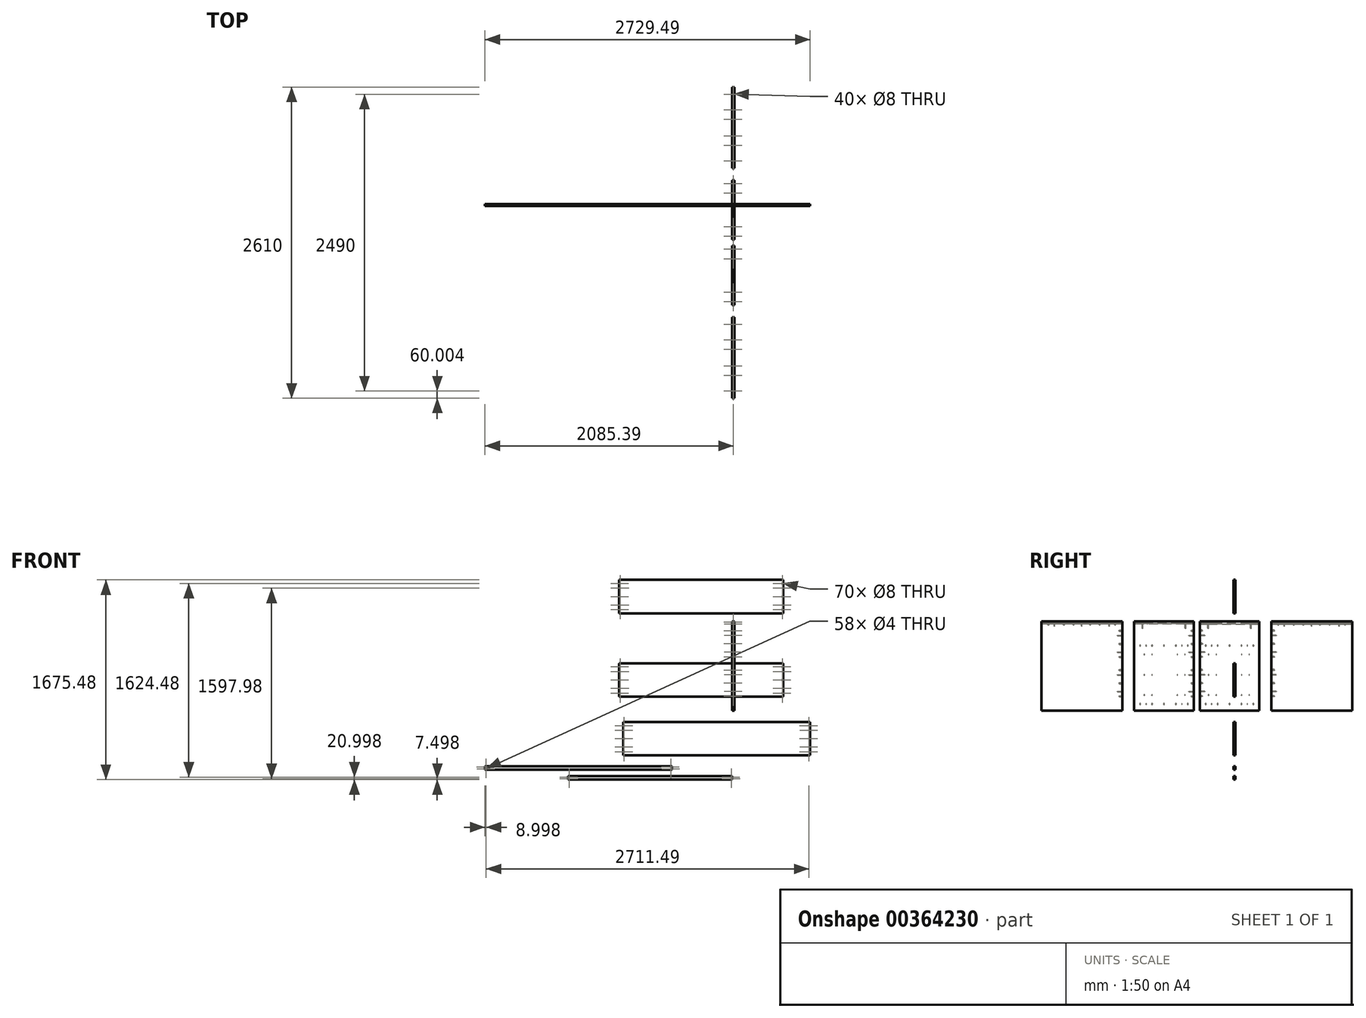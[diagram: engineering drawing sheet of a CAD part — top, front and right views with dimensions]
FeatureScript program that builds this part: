
annotation { "Feature Type Name" : "Feature", "Feature Type Description" : "" }
export const myFeature = defineFeature(function(context is Context, id is Id, definition is map)
    precondition{}
    {
        {
            var Q0;
            Q0=qCreatedBy(makeId("Right.planeOp"),FACE);
            var sketch = newSketch(context, id + "F0", { "sketchPlane" : qUnion([Q0])});
            skLineSegment(sketch, "E0.bottom", {"start": v(-300.67, 437.5) * mm, "end": v(199.33, 437.5) * mm});
            skLineSegment(sketch, "E0.top", {"start": v(-300.67, -312.5) * mm, "end": v(199.33, -312.5) * mm});
            skLineSegment(sketch, "E0.left", {"start": v(-300.67, 437.5) * mm, "end": v(-300.67, -312.5) * mm});
            skLineSegment(sketch, "E0.right", {"start": v(199.33, 437.5) * mm, "end": v(199.33, -312.5) * mm});
            skSolve(sketch);
        }
        {
            var Q0;
            Q0=makeQuery(id+"F0.imprint","IMPRINT",FACE,{"disambiguationData":[TD([[makeQuery(id+"F0.imprint","IMPRINT",EDGE,{"derivedFrom":sQuery(id+"F0.wireOp",EDGE,"E0.bottom")}),-1.0]])]});
            var sketch = newSketch(context, id + "F1", { "sketchPlane" : qUnion([Q0])});
            skLineSegment(sketch, "E1", {"start": v(-300.67, -257.5) * mm, "end": v(199.33, -257.5) * mm, "construction": true});
            skPoint(sketch, "E2", {"position": v(-250.67, -257.5) * mm});
            skPoint(sketch, "E3.1.0.0", {"position": v(-150.67, -257.5) * mm});
            skPoint(sketch, "E3.2.0.0", {"position": v(-50.67, -257.5) * mm});
            skPoint(sketch, "E3.3.0.0", {"position": v(49.33, -257.5) * mm});
            skPoint(sketch, "E3.4.0.0", {"position": v(149.33, -257.5) * mm});
            skLineSegment(sketch, "E3.direction1", {"start": v(-250.67, -257.5) * mm, "end": v(-150.67, -257.5) * mm, "construction": true});
            skPoint(sketch, "E4", {"position": v(99.33, -257.5) * mm});
            skPoint(sketch, "E5", {"position": v(-200.67, -257.5) * mm});
            skPoint(sketch, "E6.0.1.0", {"position": v(99.33, 232.5) * mm});
            skPoint(sketch, "E6.0.1.1", {"position": v(-150.67, 232.5) * mm});
            skPoint(sketch, "E6.0.1.2", {"position": v(-250.67, 232.5) * mm});
            skLineSegment(sketch, "E6.0.1.3", {"start": v(-300.67, 232.5) * mm, "end": v(199.33, 232.5) * mm, "construction": true});
            skPoint(sketch, "E6.0.1.4", {"position": v(-50.67, 232.5) * mm});
            skPoint(sketch, "E6.0.1.5", {"position": v(149.33, 232.5) * mm});
            skPoint(sketch, "E6.0.1.6", {"position": v(-200.67, 232.5) * mm});
            skPoint(sketch, "E6.0.1.7", {"position": v(49.33, 232.5) * mm});
            skLineSegment(sketch, "E6.0.1.8", {"start": v(-250.67, 232.5) * mm, "end": v(-150.67, 232.5) * mm, "construction": true});
            skPoint(sketch, "E6.1.0.0", {"position": v(124.33, -257.5) * mm});
            skPoint(sketch, "E6.1.0.1", {"position": v(-125.67, -257.5) * mm});
            skPoint(sketch, "E6.1.0.2", {"position": v(-225.67, -257.5) * mm});
            skLineSegment(sketch, "E6.1.0.3", {"start": v(-275.67, -257.5) * mm, "end": v(224.33, -257.5) * mm, "construction": true});
            skPoint(sketch, "E6.1.0.4", {"position": v(-25.67, -257.5) * mm});
            skPoint(sketch, "E6.1.0.5", {"position": v(174.33, -257.5) * mm});
            skPoint(sketch, "E6.1.0.6", {"position": v(-175.67, -257.5) * mm});
            skPoint(sketch, "E6.1.0.7", {"position": v(74.33, -257.5) * mm});
            skLineSegment(sketch, "E6.1.0.8", {"start": v(-225.67, -257.5) * mm, "end": v(-125.67, -257.5) * mm, "construction": true});
            skPoint(sketch, "E6.1.1.0", {"position": v(124.33, 232.5) * mm});
            skPoint(sketch, "E6.1.1.1", {"position": v(-125.67, 232.5) * mm});
            skPoint(sketch, "E6.1.1.2", {"position": v(-225.67, 232.5) * mm});
            skLineSegment(sketch, "E6.1.1.3", {"start": v(-275.67, 232.5) * mm, "end": v(224.33, 232.5) * mm, "construction": true});
            skPoint(sketch, "E6.1.1.4", {"position": v(-25.67, 232.5) * mm});
            skPoint(sketch, "E6.1.1.5", {"position": v(174.33, 232.5) * mm});
            skPoint(sketch, "E6.1.1.6", {"position": v(-175.67, 232.5) * mm});
            skPoint(sketch, "E6.1.1.7", {"position": v(74.33, 232.5) * mm});
            skLineSegment(sketch, "E6.1.1.8", {"start": v(-225.67, 232.5) * mm, "end": v(-125.67, 232.5) * mm, "construction": true});
            skPoint(sketch, "E6.2.0.1", {"position": v(-100.67, -257.5) * mm});
            skLineSegment(sketch, "E6.2.0.3", {"start": v(-250.67, -257.5) * mm, "end": v(249.33, -257.5) * mm, "construction": true});
            skPoint(sketch, "E6.2.0.4", {"position": v(-0.67, -257.5) * mm});
            skPoint(sketch, "E6.2.0.5", {"position": v(199.33, -257.5) * mm});
            skLineSegment(sketch, "E6.2.0.8", {"start": v(-200.67, -257.5) * mm, "end": v(-100.67, -257.5) * mm, "construction": true});
            skPoint(sketch, "E6.2.1.0", {"position": v(149.33, 232.5) * mm});
            skPoint(sketch, "E6.2.1.1", {"position": v(-100.67, 232.5) * mm});
            skPoint(sketch, "E6.2.1.2", {"position": v(-200.67, 232.5) * mm});
            skLineSegment(sketch, "E6.2.1.3", {"start": v(-250.67, 232.5) * mm, "end": v(249.33, 232.5) * mm, "construction": true});
            skPoint(sketch, "E6.2.1.4", {"position": v(-0.67, 232.5) * mm});
            skPoint(sketch, "E6.2.1.5", {"position": v(199.33, 232.5) * mm});
            skPoint(sketch, "E6.2.1.6", {"position": v(-150.67, 232.5) * mm});
            skPoint(sketch, "E6.2.1.7", {"position": v(99.33, 232.5) * mm});
            skLineSegment(sketch, "E6.2.1.8", {"start": v(-200.67, 232.5) * mm, "end": v(-100.67, 232.5) * mm, "construction": true});
            skLineSegment(sketch, "E6.direction1", {"start": v(-300.67, -257.5) * mm, "end": v(-275.67, -257.5) * mm, "construction": true});
            skLineSegment(sketch, "E6.direction2", {"start": v(-300.67, -257.5) * mm, "end": v(-300.67, 232.5) * mm, "construction": true});
            skSolve(sketch);
        }
        {
            var Q0;
            Q0=makeQuery(id+"F0.imprint","IMPRINT",FACE,{"disambiguationData":[TD([[makeQuery(id+"F0.imprint","IMPRINT",EDGE,{"derivedFrom":sQuery(id+"F0.wireOp",EDGE,"E0.bottom")}),-1.0]])]});
            var sketch = newSketch(context, id + "F2", { "sketchPlane" : qUnion([Q0])});
            skLineSegment(sketch, "E7.bottom", {"start": v(-263.67, -165.1) * mm, "end": v(186.33, -165.1) * mm});
            skLineSegment(sketch, "E7.top", {"start": v(-263.67, -199.9) * mm, "end": v(186.33, -199.9) * mm});
            skLineSegment(sketch, "E7.left", {"start": v(-263.67, -165.1) * mm, "end": v(-263.67, -199.9) * mm});
            skLineSegment(sketch, "E7.right", {"start": v(186.33, -165.1) * mm, "end": v(186.33, -199.9) * mm});
            skLineSegment(sketch, "E8", {"start": v(186.33, -182.5) * mm, "end": v(-263.67, -182.5) * mm, "construction": true});
            skCircle(sketch, "E9", {"center": v(114.63, -182.5) * mm, "radius": 2.5 * mm});
            skCircle(sketch, "E10", {"center": v(-226.42, -182.5) * mm, "radius": 2.5 * mm});
            skCircle(sketch, "E11", {"center": v(-162.42, -182.5) * mm, "radius": 2.5 * mm});
            skCircle(sketch, "E12", {"center": v(50.63, -182.5) * mm, "radius": 2.5 * mm});
            skCircle(sketch, "E13", {"center": v(-243.67, -182.5) * mm, "radius": 2.25 * mm});
            skLineSegment(sketch, "E14.bottom", {"start": v(134.63, -180.2) * mm, "end": v(125.23, -180.2) * mm});
            skLineSegment(sketch, "E14.top", {"start": v(134.63, -184.8) * mm, "end": v(125.23, -184.8) * mm});
            skLineSegment(sketch, "E14.left", {"start": v(134.63, -180.2) * mm, "end": v(134.63, -184.8) * mm});
            skLineSegment(sketch, "E14.right", {"start": v(125.23, -180.2) * mm, "end": v(125.23, -184.8) * mm});
            skPoint(sketch, "E14.middle", {"position": v(129.93, -182.5) * mm});
            skLineSegment(sketch, "E15.bottom", {"start": v(159.33, -180.2) * mm, "end": v(149.93, -180.2) * mm});
            skLineSegment(sketch, "E15.top", {"start": v(159.33, -184.8) * mm, "end": v(149.93, -184.8) * mm});
            skLineSegment(sketch, "E15.left", {"start": v(159.33, -180.2) * mm, "end": v(159.33, -184.8) * mm});
            skLineSegment(sketch, "E15.right", {"start": v(149.93, -180.2) * mm, "end": v(149.93, -184.8) * mm});
            skPoint(sketch, "E15.middle", {"position": v(154.63, -182.5) * mm});
            skLineSegment(sketch, "E16.bottom", {"start": v(70.63, -180.2) * mm, "end": v(61.23, -180.2) * mm});
            skLineSegment(sketch, "E16.top", {"start": v(70.63, -184.8) * mm, "end": v(61.23, -184.8) * mm});
            skLineSegment(sketch, "E16.left", {"start": v(70.63, -180.2) * mm, "end": v(70.63, -184.8) * mm});
            skLineSegment(sketch, "E16.right", {"start": v(61.23, -180.2) * mm, "end": v(61.23, -184.8) * mm});
            skPoint(sketch, "E16.middle", {"position": v(65.93, -182.5) * mm});
            skLineSegment(sketch, "E17.bottom", {"start": v(96.43, -180.2) * mm, "end": v(87.03, -180.2) * mm});
            skLineSegment(sketch, "E17.top", {"start": v(96.43, -184.8) * mm, "end": v(87.03, -184.8) * mm});
            skLineSegment(sketch, "E17.left", {"start": v(96.43, -180.2) * mm, "end": v(96.43, -184.8) * mm});
            skLineSegment(sketch, "E17.right", {"start": v(87.03, -180.2) * mm, "end": v(87.03, -184.8) * mm});
            skPoint(sketch, "E17.middle", {"position": v(91.73, -182.5) * mm});
            skLineSegment(sketch, "E18.bottom", {"start": v(-142.42, -180.2) * mm, "end": v(-151.82, -180.2) * mm});
            skLineSegment(sketch, "E18.top", {"start": v(-142.42, -184.8) * mm, "end": v(-151.82, -184.8) * mm});
            skLineSegment(sketch, "E18.left", {"start": v(-142.42, -180.2) * mm, "end": v(-142.42, -184.8) * mm});
            skLineSegment(sketch, "E18.right", {"start": v(-151.82, -180.2) * mm, "end": v(-151.82, -184.8) * mm});
            skPoint(sketch, "E18.middle", {"position": v(-147.12, -182.5) * mm});
            skLineSegment(sketch, "E19.bottom", {"start": v(-117.72, -180.2) * mm, "end": v(-127.12, -180.2) * mm});
            skLineSegment(sketch, "E19.top", {"start": v(-117.72, -184.8) * mm, "end": v(-127.12, -184.8) * mm});
            skLineSegment(sketch, "E19.left", {"start": v(-117.72, -180.2) * mm, "end": v(-117.72, -184.8) * mm});
            skLineSegment(sketch, "E19.right", {"start": v(-127.12, -180.2) * mm, "end": v(-127.12, -184.8) * mm});
            skPoint(sketch, "E19.middle", {"position": v(-122.42, -182.5) * mm});
            skLineSegment(sketch, "E20.bottom", {"start": v(-206.42, -180.2) * mm, "end": v(-215.82, -180.2) * mm});
            skLineSegment(sketch, "E20.top", {"start": v(-206.42, -184.8) * mm, "end": v(-215.82, -184.8) * mm});
            skLineSegment(sketch, "E20.left", {"start": v(-206.42, -180.2) * mm, "end": v(-206.42, -184.8) * mm});
            skLineSegment(sketch, "E20.right", {"start": v(-215.82, -180.2) * mm, "end": v(-215.82, -184.8) * mm});
            skPoint(sketch, "E20.middle", {"position": v(-211.12, -182.5) * mm});
            skLineSegment(sketch, "E21.bottom", {"start": v(-180.62, -180.2) * mm, "end": v(-190.02, -180.2) * mm});
            skLineSegment(sketch, "E21.top", {"start": v(-180.62, -184.8) * mm, "end": v(-190.02, -184.8) * mm});
            skLineSegment(sketch, "E21.left", {"start": v(-180.62, -180.2) * mm, "end": v(-180.62, -184.8) * mm});
            skLineSegment(sketch, "E21.right", {"start": v(-190.02, -180.2) * mm, "end": v(-190.02, -184.8) * mm});
            skPoint(sketch, "E21.middle", {"position": v(-185.32, -182.5) * mm});
            skLineSegment(sketch, "E22.0.1.0", {"start": v(186.33, 4.9) * mm, "end": v(186.33, -29.9) * mm});
            skPoint(sketch, "E22.0.1.1", {"position": v(-147.12, -12.5) * mm});
            skPoint(sketch, "E22.0.1.2", {"position": v(91.73, -12.5) * mm});
            skLineSegment(sketch, "E22.0.1.3", {"start": v(186.33, -12.5) * mm, "end": v(-263.67, -12.5) * mm, "construction": true});
            skPoint(sketch, "E22.0.1.4", {"position": v(-211.12, -12.5) * mm});
            skPoint(sketch, "E22.0.1.5", {"position": v(-185.32, -12.5) * mm});
            skLineSegment(sketch, "E22.0.1.6", {"start": v(-263.67, 4.9) * mm, "end": v(-263.67, -29.9) * mm});
            skLineSegment(sketch, "E22.0.1.7", {"start": v(-263.67, 4.9) * mm, "end": v(186.33, 4.9) * mm});
            skPoint(sketch, "E22.0.1.8", {"position": v(-122.42, -12.5) * mm});
            skPoint(sketch, "E22.0.1.9", {"position": v(154.63, -12.5) * mm});
            skPoint(sketch, "E22.0.1.10", {"position": v(129.93, -12.5) * mm});
            skLineSegment(sketch, "E22.0.1.11", {"start": v(-263.67, -29.9) * mm, "end": v(186.33, -29.9) * mm});
            skPoint(sketch, "E22.0.1.12", {"position": v(65.93, -12.5) * mm});
            skCircle(sketch, "E22.0.1.13", {"center": v(114.63, -12.5) * mm, "radius": 2.5 * mm});
            skCircle(sketch, "E22.0.1.14", {"center": v(-162.42, -12.5) * mm, "radius": 2.5 * mm});
            skCircle(sketch, "E22.0.1.15", {"center": v(-243.67, -12.5) * mm, "radius": 2.25 * mm});
            skCircle(sketch, "E22.0.1.16", {"center": v(-226.42, -12.5) * mm, "radius": 2.5 * mm});
            skCircle(sketch, "E22.0.1.17", {"center": v(50.63, -12.5) * mm, "radius": 2.5 * mm});
            skLineSegment(sketch, "E22.0.1.18", {"start": v(96.43, -10.2) * mm, "end": v(96.43, -14.8) * mm});
            skLineSegment(sketch, "E22.0.1.19", {"start": v(159.33, -10.2) * mm, "end": v(159.33, -14.8) * mm});
            skLineSegment(sketch, "E22.0.1.20", {"start": v(96.43, -14.8) * mm, "end": v(87.03, -14.8) * mm});
            skLineSegment(sketch, "E22.0.1.21", {"start": v(-180.62, -10.2) * mm, "end": v(-180.62, -14.8) * mm});
            skLineSegment(sketch, "E22.0.1.22", {"start": v(-117.72, -10.2) * mm, "end": v(-117.72, -14.8) * mm});
            skLineSegment(sketch, "E22.0.1.23", {"start": v(134.63, -14.8) * mm, "end": v(125.23, -14.8) * mm});
            skLineSegment(sketch, "E22.0.1.24", {"start": v(134.63, -10.2) * mm, "end": v(125.23, -10.2) * mm});
            skLineSegment(sketch, "E22.0.1.25", {"start": v(87.03, -10.2) * mm, "end": v(87.03, -14.8) * mm});
            skLineSegment(sketch, "E22.0.1.26", {"start": v(149.93, -10.2) * mm, "end": v(149.93, -14.8) * mm});
            skLineSegment(sketch, "E22.0.1.27", {"start": v(125.23, -10.2) * mm, "end": v(125.23, -14.8) * mm});
            skLineSegment(sketch, "E22.0.1.28", {"start": v(96.43, -10.2) * mm, "end": v(87.03, -10.2) * mm});
            skLineSegment(sketch, "E22.0.1.29", {"start": v(159.33, -14.8) * mm, "end": v(149.93, -14.8) * mm});
            skLineSegment(sketch, "E22.0.1.30", {"start": v(-190.02, -10.2) * mm, "end": v(-190.02, -14.8) * mm});
            skLineSegment(sketch, "E22.0.1.31", {"start": v(-180.62, -14.8) * mm, "end": v(-190.02, -14.8) * mm});
            skLineSegment(sketch, "E22.0.1.32", {"start": v(-151.82, -10.2) * mm, "end": v(-151.82, -14.8) * mm});
            skLineSegment(sketch, "E22.0.1.33", {"start": v(-180.62, -10.2) * mm, "end": v(-190.02, -10.2) * mm});
            skLineSegment(sketch, "E22.0.1.34", {"start": v(159.33, -10.2) * mm, "end": v(149.93, -10.2) * mm});
            skLineSegment(sketch, "E22.0.1.35", {"start": v(134.63, -10.2) * mm, "end": v(134.63, -14.8) * mm});
            skLineSegment(sketch, "E22.0.1.36", {"start": v(-142.42, -14.8) * mm, "end": v(-151.82, -14.8) * mm});
            skLineSegment(sketch, "E22.0.1.37", {"start": v(70.63, -10.2) * mm, "end": v(70.63, -14.8) * mm});
            skLineSegment(sketch, "E22.0.1.38", {"start": v(-142.42, -10.2) * mm, "end": v(-151.82, -10.2) * mm});
            skLineSegment(sketch, "E22.0.1.39", {"start": v(-117.72, -14.8) * mm, "end": v(-127.12, -14.8) * mm});
            skLineSegment(sketch, "E22.0.1.40", {"start": v(70.63, -14.8) * mm, "end": v(61.23, -14.8) * mm});
            skLineSegment(sketch, "E22.0.1.41", {"start": v(-127.12, -10.2) * mm, "end": v(-127.12, -14.8) * mm});
            skLineSegment(sketch, "E22.0.1.42", {"start": v(-117.72, -10.2) * mm, "end": v(-127.12, -10.2) * mm});
            skLineSegment(sketch, "E22.0.1.43", {"start": v(-206.42, -14.8) * mm, "end": v(-215.82, -14.8) * mm});
            skLineSegment(sketch, "E22.0.1.44", {"start": v(70.63, -10.2) * mm, "end": v(61.23, -10.2) * mm});
            skLineSegment(sketch, "E22.0.1.45", {"start": v(61.23, -10.2) * mm, "end": v(61.23, -14.8) * mm});
            skLineSegment(sketch, "E22.0.1.46", {"start": v(-206.42, -10.2) * mm, "end": v(-215.82, -10.2) * mm});
            skLineSegment(sketch, "E22.0.1.47", {"start": v(-215.82, -10.2) * mm, "end": v(-215.82, -14.8) * mm});
            skLineSegment(sketch, "E22.0.1.48", {"start": v(-206.42, -10.2) * mm, "end": v(-206.42, -14.8) * mm});
            skLineSegment(sketch, "E22.0.1.49", {"start": v(-142.42, -10.2) * mm, "end": v(-142.42, -14.8) * mm});
            skLineSegment(sketch, "E22.0.2.0", {"start": v(186.33, 174.9) * mm, "end": v(186.33, 140.1) * mm});
            skPoint(sketch, "E22.0.2.1", {"position": v(-147.12, 157.5) * mm});
            skPoint(sketch, "E22.0.2.2", {"position": v(91.73, 157.5) * mm});
            skLineSegment(sketch, "E22.0.2.3", {"start": v(186.33, 157.5) * mm, "end": v(-263.67, 157.5) * mm, "construction": true});
            skPoint(sketch, "E22.0.2.4", {"position": v(-211.12, 157.5) * mm});
            skPoint(sketch, "E22.0.2.5", {"position": v(-185.32, 157.5) * mm});
            skLineSegment(sketch, "E22.0.2.6", {"start": v(-263.67, 174.9) * mm, "end": v(-263.67, 140.1) * mm});
            skLineSegment(sketch, "E22.0.2.7", {"start": v(-263.67, 174.9) * mm, "end": v(186.33, 174.9) * mm});
            skPoint(sketch, "E22.0.2.8", {"position": v(-122.42, 157.5) * mm});
            skPoint(sketch, "E22.0.2.9", {"position": v(154.63, 157.5) * mm});
            skPoint(sketch, "E22.0.2.10", {"position": v(129.93, 157.5) * mm});
            skLineSegment(sketch, "E22.0.2.11", {"start": v(-263.67, 140.1) * mm, "end": v(186.33, 140.1) * mm});
            skPoint(sketch, "E22.0.2.12", {"position": v(65.93, 157.5) * mm});
            skCircle(sketch, "E22.0.2.13", {"center": v(114.63, 157.5) * mm, "radius": 2.5 * mm});
            skCircle(sketch, "E22.0.2.14", {"center": v(-162.42, 157.5) * mm, "radius": 2.5 * mm});
            skCircle(sketch, "E22.0.2.15", {"center": v(-243.67, 157.5) * mm, "radius": 2.25 * mm});
            skCircle(sketch, "E22.0.2.16", {"center": v(-226.42, 157.5) * mm, "radius": 2.5 * mm});
            skCircle(sketch, "E22.0.2.17", {"center": v(50.63, 157.5) * mm, "radius": 2.5 * mm});
            skLineSegment(sketch, "E22.0.2.18", {"start": v(96.43, 159.8) * mm, "end": v(96.43, 155.2) * mm});
            skLineSegment(sketch, "E22.0.2.19", {"start": v(159.33, 159.8) * mm, "end": v(159.33, 155.2) * mm});
            skLineSegment(sketch, "E22.0.2.20", {"start": v(96.43, 155.2) * mm, "end": v(87.03, 155.2) * mm});
            skLineSegment(sketch, "E22.0.2.21", {"start": v(-180.62, 159.8) * mm, "end": v(-180.62, 155.2) * mm});
            skLineSegment(sketch, "E22.0.2.22", {"start": v(-117.72, 159.8) * mm, "end": v(-117.72, 155.2) * mm});
            skLineSegment(sketch, "E22.0.2.23", {"start": v(134.63, 155.2) * mm, "end": v(125.23, 155.2) * mm});
            skLineSegment(sketch, "E22.0.2.24", {"start": v(134.63, 159.8) * mm, "end": v(125.23, 159.8) * mm});
            skLineSegment(sketch, "E22.0.2.25", {"start": v(87.03, 159.8) * mm, "end": v(87.03, 155.2) * mm});
            skLineSegment(sketch, "E22.0.2.26", {"start": v(149.93, 159.8) * mm, "end": v(149.93, 155.2) * mm});
            skLineSegment(sketch, "E22.0.2.27", {"start": v(125.23, 159.8) * mm, "end": v(125.23, 155.2) * mm});
            skLineSegment(sketch, "E22.0.2.28", {"start": v(96.43, 159.8) * mm, "end": v(87.03, 159.8) * mm});
            skLineSegment(sketch, "E22.0.2.29", {"start": v(159.33, 155.2) * mm, "end": v(149.93, 155.2) * mm});
            skLineSegment(sketch, "E22.0.2.30", {"start": v(-190.02, 159.8) * mm, "end": v(-190.02, 155.2) * mm});
            skLineSegment(sketch, "E22.0.2.31", {"start": v(-180.62, 155.2) * mm, "end": v(-190.02, 155.2) * mm});
            skLineSegment(sketch, "E22.0.2.32", {"start": v(-151.82, 159.8) * mm, "end": v(-151.82, 155.2) * mm});
            skLineSegment(sketch, "E22.0.2.33", {"start": v(-180.62, 159.8) * mm, "end": v(-190.02, 159.8) * mm});
            skLineSegment(sketch, "E22.0.2.34", {"start": v(159.33, 159.8) * mm, "end": v(149.93, 159.8) * mm});
            skLineSegment(sketch, "E22.0.2.35", {"start": v(134.63, 159.8) * mm, "end": v(134.63, 155.2) * mm});
            skLineSegment(sketch, "E22.0.2.36", {"start": v(-142.42, 155.2) * mm, "end": v(-151.82, 155.2) * mm});
            skLineSegment(sketch, "E22.0.2.37", {"start": v(70.63, 159.8) * mm, "end": v(70.63, 155.2) * mm});
            skLineSegment(sketch, "E22.0.2.38", {"start": v(-142.42, 159.8) * mm, "end": v(-151.82, 159.8) * mm});
            skLineSegment(sketch, "E22.0.2.39", {"start": v(-117.72, 155.2) * mm, "end": v(-127.12, 155.2) * mm});
            skLineSegment(sketch, "E22.0.2.40", {"start": v(70.63, 155.2) * mm, "end": v(61.23, 155.2) * mm});
            skLineSegment(sketch, "E22.0.2.41", {"start": v(-127.12, 159.8) * mm, "end": v(-127.12, 155.2) * mm});
            skLineSegment(sketch, "E22.0.2.42", {"start": v(-117.72, 159.8) * mm, "end": v(-127.12, 159.8) * mm});
            skLineSegment(sketch, "E22.0.2.43", {"start": v(-206.42, 155.2) * mm, "end": v(-215.82, 155.2) * mm});
            skLineSegment(sketch, "E22.0.2.44", {"start": v(70.63, 159.8) * mm, "end": v(61.23, 159.8) * mm});
            skLineSegment(sketch, "E22.0.2.45", {"start": v(61.23, 159.8) * mm, "end": v(61.23, 155.2) * mm});
            skLineSegment(sketch, "E22.0.2.46", {"start": v(-206.42, 159.8) * mm, "end": v(-215.82, 159.8) * mm});
            skLineSegment(sketch, "E22.0.2.47", {"start": v(-215.82, 159.8) * mm, "end": v(-215.82, 155.2) * mm});
            skLineSegment(sketch, "E22.0.2.48", {"start": v(-206.42, 159.8) * mm, "end": v(-206.42, 155.2) * mm});
            skLineSegment(sketch, "E22.0.2.49", {"start": v(-142.42, 159.8) * mm, "end": v(-142.42, 155.2) * mm});
            skLineSegment(sketch, "E22.direction1", {"start": v(-263.67, -199.9) * mm, "end": v(-238.67, -199.9) * mm, "construction": true});
            skLineSegment(sketch, "E22.direction2", {"start": v(-263.67, -199.9) * mm, "end": v(-263.67, -29.9) * mm, "construction": true});
            skSolve(sketch);
        }
        {
            var Q0;
            Q0 = qSketchRegion(id + "F0", true);
            extrude(context, id + "F3", {"entities" : qUnion([Q0]), "depth" : 18 * mm});
        }
        {
            var Q0;
            Q0=sQuery(id+"F2.wireOp",VERTEX,"E9.center");
            var Q1;
            Q1=sQuery(id+"F2.wireOp",VERTEX,"E12.center");
            var Q2;
            Q2=sQuery(id+"F2.wireOp",VERTEX,"E11.center");
            var Q3;
            Q3=sQuery(id+"F2.wireOp",VERTEX,"E10.center");
            var Q4;
            Q4=sQuery(id+"F2.wireOp",VERTEX,"E22.0.1.13.center");
            var Q5;
            Q5=sQuery(id+"F2.wireOp",VERTEX,"E22.0.1.17.center");
            var Q6;
            Q6=sQuery(id+"F2.wireOp",VERTEX,"E22.0.1.14.center");
            var Q7;
            Q7=sQuery(id+"F2.wireOp",VERTEX,"E22.0.1.16.center");
            var Q8;
            Q8=sQuery(id+"F2.wireOp",VERTEX,"E22.0.3.16.center");
            var Q9;
            Q9=sQuery(id+"F2.wireOp",VERTEX,"E22.0.2.16.center");
            var Q10;
            Q10=sQuery(id+"F2.wireOp",VERTEX,"E22.0.2.14.center");
            var Q11;
            Q11=sQuery(id+"F2.wireOp",VERTEX,"E22.0.3.14.center");
            var Q12;
            Q12=sQuery(id+"F2.wireOp",VERTEX,"E22.0.3.13.center");
            var Q13;
            Q13=sQuery(id+"F2.wireOp",VERTEX,"E22.0.2.13.center");
            var Q14;
            Q14=sQuery(id+"F2.wireOp",VERTEX,"E22.0.2.17.center");
            var Q15;
            Q15=sQuery(id+"F2.wireOp",VERTEX,"E22.0.3.17.center");
            var Q16;
            Q16=makeQuery(id+"F3.opExtrude","SWEPT_BODY",BODY,{"disambiguationData":[OSD([sQuery(id+"F0.wireOp",EDGE,"E0.bottom"),sQuery(id+"F0.wireOp",EDGE,"E0.top"),sQuery(id+"F0.wireOp",EDGE,"E0.left"),sQuery(id+"F0.wireOp",EDGE,"E0.right")])]});
            hole(context, id + "F4", {"style" : HoleStyle.SIMPLE, "endStyle" : HoleEndStyle.BLIND, "oppositeDirection" : true, "holeDiameter" : 4.5 * mm, "holeDepth" : 10 * mm, "isTappedThrough" : true, "tappedDepth" : 12 * mm, "tapClearance" : 3, "startFromSketch" : true, "locations" : qUnion([Q0, Q1, Q2, Q3, Q4, Q5, Q6, Q7, Q8, Q9, Q10, Q11, Q12, Q13, Q14, Q15]), "scope" : qUnion([Q16])});
        }
        {
            var Q0;
            Q0=sQuery(id+"F1.wireOp",VERTEX,"E2");
            var Q1;
            Q1=sQuery(id+"F1.wireOp",VERTEX,"E3.1.0.0");
            var Q2;
            Q2=sQuery(id+"F1.wireOp",VERTEX,"E3.2.0.0");
            var Q3;
            Q3=sQuery(id+"F1.wireOp",VERTEX,"E3.3.0.0");
            var Q4;
            Q4=sQuery(id+"F1.wireOp",VERTEX,"E3.4.0.0");
            var Q5;
            Q5=sQuery(id+"F1.wireOp",VERTEX,"E6.2.1.0");
            var Q6;
            Q6=sQuery(id+"F1.wireOp",VERTEX,"E6.0.1.7");
            var Q7;
            Q7=sQuery(id+"F1.wireOp",VERTEX,"E6.0.1.4");
            var Q8;
            Q8=sQuery(id+"F1.wireOp",VERTEX,"E6.0.1.2");
            var Q9;
            Q9=sQuery(id+"F1.wireOp",VERTEX,"E6.2.1.6");
            var Q10;
            Q10=makeQuery(id+"F3.opExtrude","SWEPT_BODY",BODY,{"disambiguationData":[OSD([sQuery(id+"F0.wireOp",EDGE,"E0.bottom"),sQuery(id+"F0.wireOp",EDGE,"E0.top"),sQuery(id+"F0.wireOp",EDGE,"E0.left"),sQuery(id+"F0.wireOp",EDGE,"E0.right")])]});
            hole(context, id + "F5", {"style" : HoleStyle.SIMPLE, "endStyle" : HoleEndStyle.BLIND, "oppositeDirection" : true, "holeDiameter" : 8 * mm, "holeDepth" : 10 * mm, "isTappedThrough" : true, "tappedDepth" : 12 * mm, "tapClearance" : 3, "startFromSketch" : true, "locations" : qUnion([Q0, Q1, Q2, Q3, Q4, Q5, Q6, Q7, Q8, Q9]), "scope" : qUnion([Q10])});
        }
        {
            var Q0;
            Q0=sQuery(id+"F1.wireOp",VERTEX,"E4");
            var Q1;
            Q1=sQuery(id+"F1.wireOp",VERTEX,"E5");
            var Q2;
            Q2=sQuery(id+"F1.wireOp",VERTEX,"E6.0.1.0");
            var Q3;
            Q3=sQuery(id+"F1.wireOp",VERTEX,"E6.2.1.2");
            var Q4;
            Q4=makeQuery(id+"F3.opExtrude","SWEPT_BODY",BODY,{"disambiguationData":[OSD([sQuery(id+"F0.wireOp",EDGE,"E0.bottom"),sQuery(id+"F0.wireOp",EDGE,"E0.top"),sQuery(id+"F0.wireOp",EDGE,"E0.left"),sQuery(id+"F0.wireOp",EDGE,"E0.right")])]});
            hole(context, id + "F6", {"style" : HoleStyle.SIMPLE, "endStyle" : HoleEndStyle.BLIND, "oppositeDirection" : true, "holeDiameter" : 5 * mm, "holeDepth" : 10 * mm, "isTappedThrough" : true, "tappedDepth" : 12 * mm, "tapClearance" : 3, "startFromSketch" : true, "locations" : qUnion([Q0, Q1, Q2, Q3]), "scope" : qUnion([Q4])});
        }
        {
            var Q0;
            Q0=qCreatedBy(makeId("Right.planeOp"),FACE);
            var sketch = newSketch(context, id + "F7", { "sketchPlane" : qUnion([Q0])});
            skLineSegment(sketch, "E23.bottom", {"start": v(979.33, 437.5) * mm, "end": v(299.33, 437.5) * mm});
            skLineSegment(sketch, "E23.top", {"start": v(979.33, -312.5) * mm, "end": v(299.33, -312.5) * mm});
            skLineSegment(sketch, "E23.left", {"start": v(979.33, 437.5) * mm, "end": v(979.33, -312.5) * mm});
            skLineSegment(sketch, "E23.right", {"start": v(299.33, 437.5) * mm, "end": v(299.33, -312.5) * mm});
            skLineSegment(sketch, "E24", {"start": v(299.33, -312.5) * mm, "end": v(199.33, -312.5) * mm, "construction": true});
            skSolve(sketch);
        }
        {
            var Q0;
            Q0=makeQuery(id+"F7.imprint","IMPRINT",FACE,{"disambiguationData":[TD([[makeQuery(id+"F7.imprint","IMPRINT",EDGE,{"derivedFrom":sQuery(id+"F7.wireOp",EDGE,"E23.bottom")}),1.0]])]});
            extrude(context, id + "F8", {"entities" : qUnion([Q0]), "depth" : 18 * mm});
        }
        {
            var Q0;
            Q0=makeQuery(id+"F8.opExtrude","SWEPT_FACE",FACE,{"disambiguationData":[OSD([sQuery(id+"F7.wireOp",EDGE,"E23.left")])]});
            var sketch = newSketch(context, id + "F9", { "sketchPlane" : qUnion([Q0])});
            skLineSegment(sketch, "E25", {"start": v(-9, 437.5) * mm, "end": v(-9, 392.5) * mm, "construction": true});
            skPoint(sketch, "E26", {"position": v(-9, 428.5) * mm});
            skPoint(sketch, "E27", {"position": v(-9, 415) * mm});
            skSolve(sketch);
        }
        {
            var Q0;
            Q0=sQuery(id+"F9.wireOp",VERTEX,"E27");
            var Q1;
            Q1=makeQuery(id+"F8.opExtrude","SWEPT_BODY",BODY,{"disambiguationData":[OSD([sQuery(id+"F7.wireOp",EDGE,"E23.bottom"),sQuery(id+"F7.wireOp",EDGE,"E23.top"),sQuery(id+"F7.wireOp",EDGE,"E23.left"),sQuery(id+"F7.wireOp",EDGE,"E23.right")])]});
            hole(context, id + "F10", {"style" : HoleStyle.SIMPLE, "endStyle" : HoleEndStyle.THROUGH, "holeDiameter" : 4 * mm, "isTappedThrough" : true, "tappedDepth" : 12 * mm, "tapClearance" : 3, "locations" : qUnion([Q0]), "scope" : qUnion([Q1])});
        }
        {
            var Q0;
            Q0=sQuery(id+"F9.wireOp",VERTEX,"E26");
            var Q1;
            Q1=makeQuery(id+"F8.opExtrude","SWEPT_BODY",BODY,{"disambiguationData":[OSD([sQuery(id+"F7.wireOp",EDGE,"E23.bottom"),sQuery(id+"F7.wireOp",EDGE,"E23.top"),sQuery(id+"F7.wireOp",EDGE,"E23.left"),sQuery(id+"F7.wireOp",EDGE,"E23.right")])]});
            hole(context, id + "F11", {"style" : HoleStyle.SIMPLE, "endStyle" : HoleEndStyle.THROUGH, "holeDiameter" : 8 * mm, "isTappedThrough" : true, "tappedDepth" : 12 * mm, "tapClearance" : 3, "locations" : qUnion([Q0]), "scope" : qUnion([Q1])});
        }
        {
            var Q0;
            Q0=qCreatedBy(makeId("Front.planeOp"),FACE);
            var sketch = newSketch(context, id + "F12", { "sketchPlane" : qUnion([Q0])});
            skLineSegment(sketch, "E28.bottom", {"start": v(-916.9, -408.71) * mm, "end": v(653.1, -408.71) * mm});
            skLineSegment(sketch, "E28.top", {"start": v(-916.9, -688.71) * mm, "end": v(653.1, -688.71) * mm});
            skLineSegment(sketch, "E28.left", {"start": v(-916.9, -408.71) * mm, "end": v(-916.9, -688.71) * mm});
            skLineSegment(sketch, "E28.right", {"start": v(653.1, -408.71) * mm, "end": v(653.1, -688.71) * mm});
            skSolve(sketch);
        }
        {
            var Q0;
            Q0 = qSketchRegion(id + "F12", true);
            extrude(context, id + "F13", {"entities" : qUnion([Q0]), "operationType" : NewBodyOperationType.ADD, "depth" : 18 * mm});
        }
        {
            var Q0;
            Q0=qCreatedBy(makeId("Front.planeOp"),FACE);
            var sketch = newSketch(context, id + "F14", { "sketchPlane" : qUnion([Q0])});
            skLineSegment(sketch, "E29.0.0", {"start": v(-916.9, -408.71) * mm, "end": v(-916.9, -688.71) * mm});
            skLineSegment(sketch, "E29.0.1", {"start": v(-916.9, -688.71) * mm, "end": v(653.1, -688.71) * mm});
            skLineSegment(sketch, "E29.0.2", {"start": v(653.1, -688.71) * mm, "end": v(653.1, -408.71) * mm});
            skLineSegment(sketch, "E29.0.3", {"start": v(653.1, -408.71) * mm, "end": v(-916.9, -408.71) * mm});
            skLineSegment(sketch, "E30.bottom", {"start": v(-951.53, 83.9) * mm, "end": v(428.47, 83.9) * mm});
            skLineSegment(sketch, "E30.top", {"start": v(-951.53, -196.1) * mm, "end": v(428.47, -196.1) * mm});
            skLineSegment(sketch, "E30.left", {"start": v(-951.53, 83.9) * mm, "end": v(-951.53, -196.1) * mm});
            skLineSegment(sketch, "E30.right", {"start": v(428.47, 83.9) * mm, "end": v(428.47, -196.1) * mm});
            skSolve(sketch);
        }
        {
            var Q0;
            Q0 = qSketchRegion(id + "F14", true);
            extrude(context, id + "F15", {"entities" : qUnion([Q0]), "depth" : 18 * mm});
        }
        {
            var Q0;
            Q0=makeQuery(id+"F15.opExtrude","SWEPT_BODY",BODY,{"disambiguationData":[OSD([sQuery(id+"F14.wireOp",EDGE,"E29.0.0"),sQuery(id+"F14.wireOp",EDGE,"E29.0.1"),sQuery(id+"F14.wireOp",EDGE,"E29.0.2"),sQuery(id+"F14.wireOp",EDGE,"E29.0.3")])]});
            deleteBodies(context, id + "F16", {"entities" : qUnion([Q0])});
        }
        {
            var Q0;
            Q0=makeQuery(id+"F3.opExtrude","SWEPT_FACE",FACE,{"disambiguationData":[OSD([sQuery(id+"F0.wireOp",EDGE,"E0.bottom")])]});
            var sketch = newSketch(context, id + "F17", { "sketchPlane" : qUnion([Q0])});
            skLineSegment(sketch, "E31", {"start": v(9, 199.33) * mm, "end": v(9, -300.67) * mm, "construction": true});
            skLineSegment(sketch, "E32", {"start": v(0, -50.67) * mm, "end": v(18, -50.67) * mm, "construction": true});
            skPoint(sketch, "E33", {"position": v(9, -50.67) * mm});
            skPoint(sketch, "E34", {"position": v(9, 169.33) * mm});
            skPoint(sketch, "E35.0.1.0", {"position": v(9, 129.33) * mm});
            skPoint(sketch, "E35.0.2.0", {"position": v(9, 89.33) * mm});
            skLineSegment(sketch, "E35.direction1", {"start": v(9, 169.33) * mm, "end": v(34, 169.33) * mm, "construction": true});
            skLineSegment(sketch, "E35.direction2", {"start": v(9, 169.33) * mm, "end": v(9, 129.33) * mm, "construction": true});
            skPoint(sketch, "E36.MirrorP", {"position": v(9, -270.67) * mm});
            skPoint(sketch, "E37.MirrorP", {"position": v(9, -230.67) * mm});
            skPoint(sketch, "E38.MirrorP", {"position": v(9, -190.67) * mm});
            skSolve(sketch);
        }
        {
            var Q0;
            Q0=sQuery(id+"F17.wireOp",VERTEX,"E34");
            var Q1;
            Q1=sQuery(id+"F17.wireOp",VERTEX,"E35.0.2.0");
            var Q2;
            Q2=sQuery(id+"F17.wireOp",VERTEX,"E38.MirrorP");
            var Q3;
            Q3=sQuery(id+"F17.wireOp",VERTEX,"E36.MirrorP");
            var Q4;
            Q4=makeQuery(id+"F3.opExtrude","SWEPT_BODY",BODY,{"disambiguationData":[OSD([sQuery(id+"F0.wireOp",EDGE,"E0.bottom"),sQuery(id+"F0.wireOp",EDGE,"E0.top"),sQuery(id+"F0.wireOp",EDGE,"E0.left"),sQuery(id+"F0.wireOp",EDGE,"E0.right")])]});
            hole(context, id + "F18", {"style" : HoleStyle.SIMPLE, "endStyle" : HoleEndStyle.BLIND, "holeDiameter" : 8 * mm, "holeDepth" : 20 * mm, "isTappedThrough" : true, "tappedDepth" : 12 * mm, "tapClearance" : 3, "startFromSketch" : true, "locations" : qUnion([Q0, Q1, Q2, Q3]), "scope" : qUnion([Q4])});
        }
        {
            var Q0;
            Q0=sQuery(id+"F17.wireOp",VERTEX,"E35.0.1.0");
            var Q1;
            Q1=sQuery(id+"F17.wireOp",VERTEX,"E37.MirrorP");
            var Q2;
            Q2=makeQuery(id+"F3.opExtrude","SWEPT_BODY",BODY,{"disambiguationData":[OSD([sQuery(id+"F0.wireOp",EDGE,"E0.bottom"),sQuery(id+"F0.wireOp",EDGE,"E0.top"),sQuery(id+"F0.wireOp",EDGE,"E0.left"),sQuery(id+"F0.wireOp",EDGE,"E0.right")])]});
            hole(context, id + "F19", {"style" : HoleStyle.SIMPLE, "endStyle" : HoleEndStyle.BLIND, "holeDiameter" : 5 * mm, "holeDepth" : 60 * mm, "isTappedThrough" : true, "tappedDepth" : 12 * mm, "tapClearance" : 3, "startFromSketch" : true, "locations" : qUnion([Q0, Q1]), "scope" : qUnion([Q2])});
        }
        {
            var Q0;
            Q0=makeQuery(id+"F8.opExtrude","SWEPT_FACE",FACE,{"disambiguationData":[OSD([sQuery(id+"F7.wireOp",EDGE,"E23.bottom")])]});
            var sketch = newSketch(context, id + "F20", { "sketchPlane" : qUnion([Q0])});
            skLineSegment(sketch, "E39", {"start": v(9, 979.33) * mm, "end": v(9, 299.33) * mm, "construction": true});
            skPoint(sketch, "E40", {"position": v(9, 359.33) * mm});
            skPoint(sketch, "E41", {"position": v(9, 409.33) * mm});
            skPoint(sketch, "E42", {"position": v(9, 489.33) * mm});
            skPoint(sketch, "E43", {"position": v(9, 639.33) * mm});
            skPoint(sketch, "E44", {"position": v(9, 569.33) * mm});
            skLineSegment(sketch, "E45", {"start": v(-174.96, 639.33) * mm, "end": v(192.1, 639.33) * mm, "construction": true});
            skPoint(sketch, "E46.MirrorP", {"position": v(9, 709.33) * mm});
            skPoint(sketch, "E47.MirrorP", {"position": v(9, 789.33) * mm});
            skPoint(sketch, "E48.MirrorP", {"position": v(9, 869.33) * mm});
            skPoint(sketch, "E49.MirrorP", {"position": v(9, 919.33) * mm});
            skSolve(sketch);
        }
        {
            var Q0;
            Q0=sQuery(id+"F20.wireOp",VERTEX,"E48.MirrorP");
            var Q1;
            Q1=sQuery(id+"F20.wireOp",VERTEX,"E43");
            var Q2;
            Q2=sQuery(id+"F20.wireOp",VERTEX,"E41");
            var Q3;
            Q3=makeQuery(id+"F8.opExtrude","SWEPT_BODY",BODY,{"disambiguationData":[OSD([sQuery(id+"F7.wireOp",EDGE,"E23.bottom"),sQuery(id+"F7.wireOp",EDGE,"E23.top"),sQuery(id+"F7.wireOp",EDGE,"E23.left"),sQuery(id+"F7.wireOp",EDGE,"E23.right")])]});
            hole(context, id + "F21", {"style" : HoleStyle.SIMPLE, "endStyle" : HoleEndStyle.BLIND, "holeDiameter" : 4 * mm, "holeDepth" : 40 * mm, "isTappedThrough" : true, "tappedDepth" : 12 * mm, "tapClearance" : 3, "locations" : qUnion([Q0, Q1, Q2]), "scope" : qUnion([Q3])});
        }
        {
            var Q0;
            Q0=sQuery(id+"F20.wireOp",VERTEX,"E40");
            var Q1;
            Q1=sQuery(id+"F20.wireOp",VERTEX,"E42");
            var Q2;
            Q2=sQuery(id+"F20.wireOp",VERTEX,"E44");
            var Q3;
            Q3=sQuery(id+"F20.wireOp",VERTEX,"E46.MirrorP");
            var Q4;
            Q4=sQuery(id+"F20.wireOp",VERTEX,"E47.MirrorP");
            var Q5;
            Q5=sQuery(id+"F20.wireOp",VERTEX,"E49.MirrorP");
            var Q6;
            Q6=makeQuery(id+"F8.opExtrude","SWEPT_BODY",BODY,{"disambiguationData":[OSD([sQuery(id+"F7.wireOp",EDGE,"E23.bottom"),sQuery(id+"F7.wireOp",EDGE,"E23.top"),sQuery(id+"F7.wireOp",EDGE,"E23.left"),sQuery(id+"F7.wireOp",EDGE,"E23.right")])]});
            hole(context, id + "F22", {"style" : HoleStyle.SIMPLE, "endStyle" : HoleEndStyle.BLIND, "holeDiameter" : 8 * mm, "holeDepth" : 30 * mm, "isTappedThrough" : true, "tappedDepth" : 12 * mm, "tapClearance" : 3, "locations" : qUnion([Q0, Q1, Q2, Q3, Q4, Q5]), "scope" : qUnion([Q6])});
        }
        {
            var Q0;
            Q0=makeQuery(id+"F3.opExtrude","SWEPT_FACE",FACE,{"disambiguationData":[OSD([sQuery(id+"F0.wireOp",EDGE,"E0.left")])]});
            cPlane(context, id + "F23", {"entities" : qUnion([Q0]), "cplaneType" : CPlaneType.OFFSET, "offset" : 25 * mm, "width" : 150 * mm, "height" : 150 * mm});
        }
        {
            var Q0;
            Q0=qCreatedBy(makeId("Front.planeOp"),FACE);
            var sketch = newSketch(context, id + "F24", { "sketchPlane" : qUnion([Q0])});
            skLineSegment(sketch, "E50.bottom", {"start": v(-2076.4, -778.8) * mm, "end": v(-506.4, -778.8) * mm});
            skLineSegment(sketch, "E50.top", {"start": v(-2076.4, -808.8) * mm, "end": v(-506.4, -808.8) * mm});
            skLineSegment(sketch, "E50.left", {"start": v(-2076.4, -778.8) * mm, "end": v(-2076.4, -808.8) * mm});
            skLineSegment(sketch, "E50.right", {"start": v(-506.4, -778.8) * mm, "end": v(-506.4, -808.8) * mm});
            skSolve(sketch);
        }
        {
            var Q0;
            Q0 = qSketchRegion(id + "F24", true);
            extrude(context, id + "F25", {"entities" : qUnion([Q0]), "depth" : 18 * mm});
        }
        {
            var Q0;
            Q0=makeQuery(id+"F25.opExtrude","CAP_FACE",FACE,{"disambiguationData":[OSD([sQuery(id+"F24.wireOp",EDGE,"E50.bottom"),sQuery(id+"F24.wireOp",EDGE,"E50.top"),sQuery(id+"F24.wireOp",EDGE,"E50.left"),sQuery(id+"F24.wireOp",EDGE,"E50.right")])],"isStart":true});
            var sketch = newSketch(context, id + "F26", { "sketchPlane" : qUnion([Q0])});
            skLineSegment(sketch, "E51", {"start": v(2067.4, -778.8) * mm, "end": v(2067.4, -808.8) * mm, "construction": true});
            skPoint(sketch, "E52", {"position": v(2067.4, -787.8) * mm});
            skPoint(sketch, "E53", {"position": v(2067.4, -801.3) * mm});
            skLineSegment(sketch, "E54", {"start": v(1291.4, -778.8) * mm, "end": v(1291.4, -808.8) * mm, "construction": true});
            skPoint(sketch, "E55.MirrorP", {"position": v(515.4, -787.8) * mm});
            skPoint(sketch, "E56.MirrorP", {"position": v(515.4, -801.3) * mm});
            skSolve(sketch);
        }
        {
            var Q0;
            Q0=sQuery(id+"F26.wireOp",VERTEX,"E52");
            var Q1;
            Q1=sQuery(id+"F26.wireOp",VERTEX,"E55.MirrorP");
            var Q2;
            Q2=makeQuery(id+"F25.opExtrude","SWEPT_BODY",BODY,{"disambiguationData":[OSD([sQuery(id+"F24.wireOp",EDGE,"E50.bottom"),sQuery(id+"F24.wireOp",EDGE,"E50.top"),sQuery(id+"F24.wireOp",EDGE,"E50.left"),sQuery(id+"F24.wireOp",EDGE,"E50.right")])]});
            hole(context, id + "F27", {"style" : HoleStyle.SIMPLE, "endStyle" : HoleEndStyle.BLIND, "holeDiameter" : 8 * mm, "holeDepth" : 10 * mm, "isTappedThrough" : true, "tappedDepth" : 12 * mm, "tapClearance" : 3, "locations" : qUnion([Q0, Q1]), "scope" : qUnion([Q2])});
        }
        {
            var Q0;
            Q0=sQuery(id+"F26.wireOp",VERTEX,"E56.MirrorP");
            var Q1;
            Q1=sQuery(id+"F26.wireOp",VERTEX,"E53");
            var Q2;
            Q2=makeQuery(id+"F25.opExtrude","SWEPT_BODY",BODY,{"disambiguationData":[OSD([sQuery(id+"F24.wireOp",EDGE,"E50.bottom"),sQuery(id+"F24.wireOp",EDGE,"E50.top"),sQuery(id+"F24.wireOp",EDGE,"E50.left"),sQuery(id+"F24.wireOp",EDGE,"E50.right")])]});
            hole(context, id + "F28", {"style" : HoleStyle.SIMPLE, "endStyle" : HoleEndStyle.BLIND, "holeDiameter" : 4 * mm, "holeDepth" : 10 * mm, "isTappedThrough" : true, "tappedDepth" : 12 * mm, "tapClearance" : 3, "locations" : qUnion([Q0, Q1]), "scope" : qUnion([Q2])});
        }
        {
            var Q0;
            Q0=qCreatedBy(makeId("Front.planeOp"),FACE);
            var sketch = newSketch(context, id + "F29", { "sketchPlane" : qUnion([Q0])});
            skLineSegment(sketch, "E57.bottom", {"start": v(0, -861.57) * mm, "end": v(-1380, -861.57) * mm});
            skLineSegment(sketch, "E57.top", {"start": v(0, -891.57) * mm, "end": v(-1380, -891.57) * mm});
            skLineSegment(sketch, "E57.left", {"start": v(0, -861.57) * mm, "end": v(0, -891.57) * mm});
            skLineSegment(sketch, "E57.right", {"start": v(-1380, -861.57) * mm, "end": v(-1380, -891.57) * mm});
            skSolve(sketch);
        }
        {
            var Q0;
            Q0 = qSketchRegion(id + "F29", true);
            extrude(context, id + "F30", {"entities" : qUnion([Q0]), "depth" : 18 * mm});
        }
        {
            var Q0;
            Q0=makeQuery(id+"F30.opExtrude","CAP_FACE",FACE,{"disambiguationData":[OSD([sQuery(id+"F29.wireOp",EDGE,"E57.bottom"),sQuery(id+"F29.wireOp",EDGE,"E57.top"),sQuery(id+"F29.wireOp",EDGE,"E57.left"),sQuery(id+"F29.wireOp",EDGE,"E57.right")])],"isStart":true});
            var sketch = newSketch(context, id + "F31", { "sketchPlane" : qUnion([Q0])});
            skLineSegment(sketch, "E58", {"start": v(1371, -861.57) * mm, "end": v(1371, -891.57) * mm, "construction": true});
            skPoint(sketch, "E59", {"position": v(1371, -870.57) * mm});
            skPoint(sketch, "E60", {"position": v(1371, -884.07) * mm});
            skLineSegment(sketch, "E61", {"start": v(690, -861.57) * mm, "end": v(690, -891.57) * mm, "construction": true});
            skPoint(sketch, "E62.MirrorP", {"position": v(9, -870.57) * mm});
            skPoint(sketch, "E63.MirrorP", {"position": v(9, -884.07) * mm});
            skSolve(sketch);
        }
        {
            var Q0;
            Q0=sQuery(id+"F31.wireOp",VERTEX,"E63.MirrorP");
            var Q1;
            Q1=sQuery(id+"F31.wireOp",VERTEX,"E60");
            var Q2;
            Q2=makeQuery(id+"F30.opExtrude","SWEPT_BODY",BODY,{"disambiguationData":[OSD([sQuery(id+"F29.wireOp",EDGE,"E57.bottom"),sQuery(id+"F29.wireOp",EDGE,"E57.top"),sQuery(id+"F29.wireOp",EDGE,"E57.left"),sQuery(id+"F29.wireOp",EDGE,"E57.right")])]});
            hole(context, id + "F32", {"style" : HoleStyle.SIMPLE, "endStyle" : HoleEndStyle.BLIND, "holeDiameter" : 4 * mm, "holeDepth" : 10 * mm, "isTappedThrough" : true, "tappedDepth" : 12 * mm, "tapClearance" : 3, "locations" : qUnion([Q0, Q1]), "scope" : qUnion([Q2])});
        }
        {
            var Q0;
            Q0=sQuery(id+"F31.wireOp",VERTEX,"E62.MirrorP");
            var Q1;
            Q1=sQuery(id+"F31.wireOp",VERTEX,"E59");
            var Q2;
            Q2=makeQuery(id+"F30.opExtrude","SWEPT_BODY",BODY,{"disambiguationData":[OSD([sQuery(id+"F29.wireOp",EDGE,"E57.bottom"),sQuery(id+"F29.wireOp",EDGE,"E57.top"),sQuery(id+"F29.wireOp",EDGE,"E57.left"),sQuery(id+"F29.wireOp",EDGE,"E57.right")])]});
            hole(context, id + "F33", {"style" : HoleStyle.SIMPLE, "endStyle" : HoleEndStyle.BLIND, "holeDiameter" : 8 * mm, "holeDepth" : 10 * mm, "isTappedThrough" : true, "tappedDepth" : 12 * mm, "tapClearance" : 3, "locations" : qUnion([Q0, Q1]), "scope" : qUnion([Q2])});
        }
        {
            var Q0;
            Q0=makeQuery(id+"F3.opExtrude","SWEPT_FACE",FACE,{"disambiguationData":[OSD([sQuery(id+"F0.wireOp",EDGE,"E0.left")])]});
            var sketch = newSketch(context, id + "F34", { "sketchPlane" : qUnion([Q0])});
            skLineSegment(sketch, "E64.bottom", {"start": v(0, 437.5) * mm, "end": v(18, 437.5) * mm});
            skLineSegment(sketch, "E64.top", {"start": v(0, -312.5) * mm, "end": v(18, -312.5) * mm});
            skLineSegment(sketch, "E64.left", {"start": v(18, 437.5) * mm, "end": v(18, -312.5) * mm});
            skLineSegment(sketch, "E64.right", {"start": v(0, 437.5) * mm, "end": v(0, -312.5) * mm});
            skLineSegment(sketch, "E65.bottom", {"start": v(0, 387.5) * mm, "end": v(18, 387.5) * mm, "construction": true});
            skLineSegment(sketch, "E65.top", {"start": v(0, 107.5) * mm, "end": v(18, 107.5) * mm, "construction": true});
            skLineSegment(sketch, "E65.left", {"start": v(18, 387.5) * mm, "end": v(18, 107.5) * mm, "construction": true});
            skLineSegment(sketch, "E65.right", {"start": v(0, 387.5) * mm, "end": v(0, 107.5) * mm, "construction": true});
            skLineSegment(sketch, "E66.bottom", {"start": v(0, -222.5) * mm, "end": v(18, -222.5) * mm, "construction": true});
            skLineSegment(sketch, "E66.top", {"start": v(0, 57.5) * mm, "end": v(18, 57.5) * mm, "construction": true});
            skLineSegment(sketch, "E66.left", {"start": v(18, -222.5) * mm, "end": v(18, 57.5) * mm, "construction": true});
            skLineSegment(sketch, "E66.right", {"start": v(0, -222.5) * mm, "end": v(0, 57.5) * mm, "construction": true});
            skLineSegment(sketch, "E67", {"start": v(9, 57.5) * mm, "end": v(9, -222.5) * mm, "construction": true});
            skPoint(sketch, "E68", {"position": v(9, 27.5) * mm});
            skPoint(sketch, "E69", {"position": v(9, -12.5) * mm});
            skPoint(sketch, "E70", {"position": v(9, -82.5) * mm});
            skPoint(sketch, "E71", {"position": v(9, -152.5) * mm});
            skPoint(sketch, "E72", {"position": v(9, -192.5) * mm});
            skLineSegment(sketch, "E73", {"start": v(9, 387.5) * mm, "end": v(9, 107.5) * mm, "construction": true});
            skPoint(sketch, "E74", {"position": v(9, 357.5) * mm});
            skPoint(sketch, "E75", {"position": v(9, 317.5) * mm});
            skPoint(sketch, "E76", {"position": v(9, 247.5) * mm});
            skPoint(sketch, "E77", {"position": v(9, 177.5) * mm});
            skPoint(sketch, "E78", {"position": v(9, 137.5) * mm});
            skSolve(sketch);
        }
        {
            var Q0;
            Q0=sQuery(id+"F34.wireOp",VERTEX,"E74");
            var Q1;
            Q1=sQuery(id+"F34.wireOp",VERTEX,"E76");
            var Q2;
            Q2=sQuery(id+"F34.wireOp",VERTEX,"E78");
            var Q3;
            Q3=sQuery(id+"F34.wireOp",VERTEX,"E72");
            var Q4;
            Q4=sQuery(id+"F34.wireOp",VERTEX,"E70");
            var Q5;
            Q5=sQuery(id+"F34.wireOp",VERTEX,"E68");
            var Q6;
            Q6=makeQuery(id+"F3.opExtrude","SWEPT_BODY",BODY,{"disambiguationData":[OSD([sQuery(id+"F0.wireOp",EDGE,"E0.bottom"),sQuery(id+"F0.wireOp",EDGE,"E0.top"),sQuery(id+"F0.wireOp",EDGE,"E0.left"),sQuery(id+"F0.wireOp",EDGE,"E0.right")])]});
            hole(context, id + "F35", {"style" : HoleStyle.SIMPLE, "endStyle" : HoleEndStyle.BLIND, "holeDiameter" : 8 * mm, "holeDepth" : 20 * mm, "isTappedThrough" : true, "tappedDepth" : 12 * mm, "tapClearance" : 3, "locations" : qUnion([Q0, Q1, Q2, Q3, Q4, Q5]), "scope" : qUnion([Q6])});
        }
        {
            var Q0;
            Q0=sQuery(id+"F34.wireOp",VERTEX,"E75");
            var Q1;
            Q1=sQuery(id+"F34.wireOp",VERTEX,"E77");
            var Q2;
            Q2=sQuery(id+"F34.wireOp",VERTEX,"E69");
            var Q3;
            Q3=sQuery(id+"F34.wireOp",VERTEX,"E71");
            var Q4;
            Q4=makeQuery(id+"F3.opExtrude","SWEPT_BODY",BODY,{"disambiguationData":[OSD([sQuery(id+"F0.wireOp",EDGE,"E0.bottom"),sQuery(id+"F0.wireOp",EDGE,"E0.top"),sQuery(id+"F0.wireOp",EDGE,"E0.left"),sQuery(id+"F0.wireOp",EDGE,"E0.right")])]});
            hole(context, id + "F36", {"style" : HoleStyle.SIMPLE, "endStyle" : HoleEndStyle.BLIND, "holeDiameter" : 4 * mm, "holeDepth" : 40 * mm, "isTappedThrough" : true, "tappedDepth" : 12 * mm, "tapClearance" : 3, "locations" : qUnion([Q0, Q1, Q2, Q3]), "scope" : qUnion([Q4])});
        }
        {
            var Q0;
            Q0=makeQuery(id+"F3.opExtrude","SWEPT_FACE",FACE,{"disambiguationData":[OSD([sQuery(id+"F0.wireOp",EDGE,"E0.right")])]});
            var sketch = newSketch(context, id + "F37", { "sketchPlane" : qUnion([Q0])});
            skLineSegment(sketch, "E79", {"start": v(-9, 437.5) * mm, "end": v(-9, 392.5) * mm, "construction": true});
            skPoint(sketch, "E80", {"position": v(-9, 428.5) * mm});
            skPoint(sketch, "E81", {"position": v(-9, 415) * mm});
            skSolve(sketch);
        }
        {
            var Q0;
            Q0=sQuery(id+"F37.wireOp",VERTEX,"E80");
            var Q1;
            Q1=makeQuery(id+"F3.opExtrude","SWEPT_BODY",BODY,{"disambiguationData":[OSD([sQuery(id+"F0.wireOp",EDGE,"E0.bottom"),sQuery(id+"F0.wireOp",EDGE,"E0.top"),sQuery(id+"F0.wireOp",EDGE,"E0.left"),sQuery(id+"F0.wireOp",EDGE,"E0.right")])]});
            hole(context, id + "F38", {"style" : HoleStyle.SIMPLE, "endStyle" : HoleEndStyle.THROUGH, "holeDiameter" : 8 * mm, "isTappedThrough" : true, "tappedDepth" : 12 * mm, "tapClearance" : 3, "locations" : qUnion([Q0]), "scope" : qUnion([Q1])});
        }
        {
            var Q0;
            Q0=sQuery(id+"F37.wireOp",VERTEX,"E81");
            var Q1;
            Q1=makeQuery(id+"F3.opExtrude","SWEPT_BODY",BODY,{"disambiguationData":[OSD([sQuery(id+"F0.wireOp",EDGE,"E0.bottom"),sQuery(id+"F0.wireOp",EDGE,"E0.top"),sQuery(id+"F0.wireOp",EDGE,"E0.left"),sQuery(id+"F0.wireOp",EDGE,"E0.right")])]});
            hole(context, id + "F39", {"style" : HoleStyle.SIMPLE, "endStyle" : HoleEndStyle.THROUGH, "holeDiameter" : 4 * mm, "isTappedThrough" : true, "tappedDepth" : 12 * mm, "tapClearance" : 3, "locations" : qUnion([Q0]), "scope" : qUnion([Q1])});
        }
        {
            var Q0;
            Q0=makeQuery(id+"F3.opExtrude","SWEPT_BODY",BODY,{"disambiguationData":[OSD([sQuery(id+"F0.wireOp",EDGE,"E0.bottom"),sQuery(id+"F0.wireOp",EDGE,"E0.top"),sQuery(id+"F0.wireOp",EDGE,"E0.left"),sQuery(id+"F0.wireOp",EDGE,"E0.right")])]});
            var Q1;
            Q1=qCreatedBy(id+"F23.planeOp",FACE);
            mirror(context, id + "F40", {"entities" : qUnion([Q0]), "mirrorPlane" : qUnion([Q1])});
        }
        {
            var Q0;
            Q0=sQuery(id+"F34.wireOp",VERTEX,"E75");
            var Q1;
            Q1=sQuery(id+"F34.wireOp",VERTEX,"E77");
            var Q2;
            Q2=sQuery(id+"F34.wireOp",VERTEX,"E69");
            var Q3;
            Q3=sQuery(id+"F34.wireOp",VERTEX,"E71");
            var Q4;
            Q4=makeQuery(id+"F8.opExtrude","SWEPT_BODY",BODY,{"disambiguationData":[OSD([sQuery(id+"F7.wireOp",EDGE,"E23.bottom"),sQuery(id+"F7.wireOp",EDGE,"E23.top"),sQuery(id+"F7.wireOp",EDGE,"E23.left"),sQuery(id+"F7.wireOp",EDGE,"E23.right")])]});
            hole(context, id + "F41", {"style" : HoleStyle.SIMPLE, "endStyle" : HoleEndStyle.BLIND, "holeDiameter" : 4 * mm, "holeDepth" : 40 * mm, "isTappedThrough" : true, "tappedDepth" : 12 * mm, "tapClearance" : 3, "locations" : qUnion([Q0, Q1, Q2, Q3]), "scope" : qUnion([Q4])});
        }
        {
            var Q0;
            Q0=sQuery(id+"F34.wireOp",VERTEX,"E74");
            var Q1;
            Q1=sQuery(id+"F34.wireOp",VERTEX,"E76");
            var Q2;
            Q2=sQuery(id+"F34.wireOp",VERTEX,"E78");
            var Q3;
            Q3=sQuery(id+"F34.wireOp",VERTEX,"E68");
            var Q4;
            Q4=sQuery(id+"F34.wireOp",VERTEX,"E70");
            var Q5;
            Q5=sQuery(id+"F34.wireOp",VERTEX,"E72");
            var Q6;
            Q6=makeQuery(id+"F8.opExtrude","SWEPT_BODY",BODY,{"disambiguationData":[OSD([sQuery(id+"F7.wireOp",EDGE,"E23.bottom"),sQuery(id+"F7.wireOp",EDGE,"E23.top"),sQuery(id+"F7.wireOp",EDGE,"E23.left"),sQuery(id+"F7.wireOp",EDGE,"E23.right")])]});
            hole(context, id + "F42", {"style" : HoleStyle.SIMPLE, "endStyle" : HoleEndStyle.BLIND, "holeDiameter" : 8 * mm, "holeDepth" : 25 * mm, "isTappedThrough" : true, "tappedDepth" : 12 * mm, "tapClearance" : 3, "locations" : qUnion([Q0, Q1, Q2, Q3, Q4, Q5]), "scope" : qUnion([Q6])});
        }
        {
            var Q0;
            Q0=makeQuery(id+"F8.opExtrude","SWEPT_BODY",BODY,{"disambiguationData":[OSD([sQuery(id+"F7.wireOp",EDGE,"E23.bottom"),sQuery(id+"F7.wireOp",EDGE,"E23.top"),sQuery(id+"F7.wireOp",EDGE,"E23.left"),sQuery(id+"F7.wireOp",EDGE,"E23.right")])]});
            var Q1;
            Q1=qCreatedBy(id+"F23.planeOp",FACE);
            mirror(context, id + "F43", {"entities" : qUnion([Q0]), "mirrorPlane" : qUnion([Q1])});
        }
        {
            var Q0;
            Q0=makeQuery(id+"F15.opExtrude","CAP_FACE",FACE,{"disambiguationData":[OSD([sQuery(id+"F14.wireOp",EDGE,"E30.bottom"),sQuery(id+"F14.wireOp",EDGE,"E30.top"),sQuery(id+"F14.wireOp",EDGE,"E30.left"),sQuery(id+"F14.wireOp",EDGE,"E30.right")])],"isStart":true});
            var sketch = newSketch(context, id + "F44", { "sketchPlane" : qUnion([Q0])});
            skLineSegment(sketch, "E82.bottom", {"start": v(933.53, 83.9) * mm, "end": v(951.53, 83.9) * mm, "construction": true});
            skLineSegment(sketch, "E82.top", {"start": v(933.53, -196.1) * mm, "end": v(951.53, -196.1) * mm, "construction": true});
            skLineSegment(sketch, "E82.left", {"start": v(933.53, 83.9) * mm, "end": v(933.53, -196.1) * mm, "construction": true});
            skLineSegment(sketch, "E82.right", {"start": v(951.53, 83.9) * mm, "end": v(951.53, -196.1) * mm, "construction": true});
            skLineSegment(sketch, "E83.bottom", {"start": v(898.9, -688.71) * mm, "end": v(916.9, -688.71) * mm, "construction": true});
            skLineSegment(sketch, "E83.top", {"start": v(898.9, -408.71) * mm, "end": v(916.9, -408.71) * mm, "construction": true});
            skLineSegment(sketch, "E83.left", {"start": v(898.9, -688.71) * mm, "end": v(898.9, -408.71) * mm, "construction": true});
            skLineSegment(sketch, "E83.right", {"start": v(916.9, -688.71) * mm, "end": v(916.9, -408.71) * mm, "construction": true});
            skLineSegment(sketch, "E84", {"start": v(907.9, -408.71) * mm, "end": v(907.9, -688.71) * mm, "construction": true});
            skPoint(sketch, "E85", {"position": v(907.9, -438.71) * mm});
            skPoint(sketch, "E86", {"position": v(907.9, -478.71) * mm});
            skPoint(sketch, "E87", {"position": v(907.9, -548.71) * mm});
            skPoint(sketch, "E88", {"position": v(907.9, -618.71) * mm});
            skPoint(sketch, "E89", {"position": v(907.9, -658.71) * mm});
            skLineSegment(sketch, "E90", {"start": v(942.53, 83.9) * mm, "end": v(942.53, -196.1) * mm, "construction": true});
            skPoint(sketch, "E91", {"position": v(942.53, 53.9) * mm});
            skPoint(sketch, "E92", {"position": v(942.53, 13.9) * mm});
            skPoint(sketch, "E93", {"position": v(942.53, -56.1) * mm});
            skPoint(sketch, "E94", {"position": v(942.53, -126.1) * mm});
            skPoint(sketch, "E95", {"position": v(942.53, -166.1) * mm});
            skLineSegment(sketch, "E96", {"start": v(131.9, -408.71) * mm, "end": v(131.9, -688.71) * mm, "construction": true});
            skLineSegment(sketch, "E97.MirrorCS", {"start": v(-635.1, -688.71) * mm, "end": v(-653.1, -688.71) * mm, "construction": true});
            skLineSegment(sketch, "E98.MirrorCS", {"start": v(-635.1, -408.71) * mm, "end": v(-653.1, -408.71) * mm, "construction": true});
            skLineSegment(sketch, "E99.MirrorCS", {"start": v(-635.1, -688.71) * mm, "end": v(-635.1, -408.71) * mm, "construction": true});
            skPoint(sketch, "E100.MirrorP", {"position": v(-644.1, -438.71) * mm});
            skLineSegment(sketch, "E101.MirrorCS", {"start": v(-653.1, -688.71) * mm, "end": v(-653.1, -408.71) * mm, "construction": true});
            skPoint(sketch, "E102.MirrorP", {"position": v(-644.1, -548.71) * mm});
            skPoint(sketch, "E103.MirrorP", {"position": v(-644.1, -618.71) * mm});
            skPoint(sketch, "E104.MirrorP", {"position": v(-644.1, -478.71) * mm});
            skLineSegment(sketch, "E105.MirrorCS", {"start": v(-644.1, -408.71) * mm, "end": v(-644.1, -688.71) * mm, "construction": true});
            skPoint(sketch, "E106.MirrorP", {"position": v(-644.1, -658.71) * mm});
            skLineSegment(sketch, "E107", {"start": v(261.53, 83.9) * mm, "end": v(261.53, -196.1) * mm, "construction": true});
            skLineSegment(sketch, "E108.MirrorCS", {"start": v(-410.47, -196.1) * mm, "end": v(-428.47, -196.1) * mm, "construction": true});
            skLineSegment(sketch, "E109.MirrorCS", {"start": v(-410.47, 83.9) * mm, "end": v(-428.47, 83.9) * mm, "construction": true});
            skPoint(sketch, "E110.MirrorP", {"position": v(-419.47, -166.1) * mm});
            skPoint(sketch, "E111.MirrorP", {"position": v(-419.47, 13.9) * mm});
            skPoint(sketch, "E112.MirrorP", {"position": v(-419.47, -126.1) * mm});
            skLineSegment(sketch, "E113.MirrorCS", {"start": v(-419.47, 83.9) * mm, "end": v(-419.47, -196.1) * mm, "construction": true});
            skPoint(sketch, "E114.MirrorP", {"position": v(-419.47, -56.1) * mm});
            skPoint(sketch, "E115.MirrorP", {"position": v(-419.47, 53.9) * mm});
            skLineSegment(sketch, "E116.MirrorCS", {"start": v(-410.47, 83.9) * mm, "end": v(-410.47, -196.1) * mm, "construction": true});
            skLineSegment(sketch, "E117.MirrorCS", {"start": v(-428.47, 83.9) * mm, "end": v(-428.47, -196.1) * mm, "construction": true});
            skSolve(sketch);
        }
        {
            var Q0;
            Q0=sQuery(id+"F44.wireOp",VERTEX,"E115.MirrorP");
            var Q1;
            Q1=sQuery(id+"F44.wireOp",VERTEX,"E114.MirrorP");
            var Q2;
            Q2=sQuery(id+"F44.wireOp",VERTEX,"E110.MirrorP");
            var Q3;
            Q3=sQuery(id+"F44.wireOp",VERTEX,"E95");
            var Q4;
            Q4=sQuery(id+"F44.wireOp",VERTEX,"E93");
            var Q5;
            Q5=sQuery(id+"F44.wireOp",VERTEX,"E91");
            var Q6;
            Q6=makeQuery(id+"F15.opExtrude","SWEPT_BODY",BODY,{"disambiguationData":[OSD([sQuery(id+"F14.wireOp",EDGE,"E30.bottom"),sQuery(id+"F14.wireOp",EDGE,"E30.top"),sQuery(id+"F14.wireOp",EDGE,"E30.left"),sQuery(id+"F14.wireOp",EDGE,"E30.right")])]});
            hole(context, id + "F45", {"style" : HoleStyle.SIMPLE, "endStyle" : HoleEndStyle.BLIND, "holeDiameter" : 8 * mm, "holeDepth" : 10 * mm, "isTappedThrough" : true, "tappedDepth" : 12 * mm, "tapClearance" : 3, "locations" : qUnion([Q0, Q1, Q2, Q3, Q4, Q5]), "scope" : qUnion([Q6])});
        }
        {
            var Q0;
            Q0=sQuery(id+"F44.wireOp",VERTEX,"E100.MirrorP");
            var Q1;
            Q1=sQuery(id+"F44.wireOp",VERTEX,"E102.MirrorP");
            var Q2;
            Q2=sQuery(id+"F44.wireOp",VERTEX,"E106.MirrorP");
            var Q3;
            Q3=sQuery(id+"F44.wireOp",VERTEX,"E85");
            var Q4;
            Q4=sQuery(id+"F44.wireOp",VERTEX,"E87");
            var Q5;
            Q5=sQuery(id+"F44.wireOp",VERTEX,"E89");
            var Q6;
            Q6=makeQuery(id+"F13.opExtrude","SWEPT_BODY",BODY,{"disambiguationData":[OSD([sQuery(id+"F12.wireOp",EDGE,"E28.bottom"),sQuery(id+"F12.wireOp",EDGE,"E28.top"),sQuery(id+"F12.wireOp",EDGE,"E28.left"),sQuery(id+"F12.wireOp",EDGE,"E28.right")])]});
            hole(context, id + "F46", {"style" : HoleStyle.SIMPLE, "endStyle" : HoleEndStyle.BLIND, "holeDiameter" : 8 * mm, "holeDepth" : 10 * mm, "isTappedThrough" : true, "tappedDepth" : 12 * mm, "tapClearance" : 3, "locations" : qUnion([Q0, Q1, Q2, Q3, Q4, Q5]), "scope" : qUnion([Q6])});
        }
        {
            var Q0;
            Q0=sQuery(id+"F44.wireOp",VERTEX,"E104.MirrorP");
            var Q1;
            Q1=sQuery(id+"F44.wireOp",VERTEX,"E103.MirrorP");
            var Q2;
            Q2=sQuery(id+"F44.wireOp",VERTEX,"E88");
            var Q3;
            Q3=sQuery(id+"F44.wireOp",VERTEX,"E86");
            var Q4;
            Q4=makeQuery(id+"F13.opExtrude","SWEPT_BODY",BODY,{"disambiguationData":[OSD([sQuery(id+"F12.wireOp",EDGE,"E28.bottom"),sQuery(id+"F12.wireOp",EDGE,"E28.top"),sQuery(id+"F12.wireOp",EDGE,"E28.left"),sQuery(id+"F12.wireOp",EDGE,"E28.right")])]});
            hole(context, id + "F47", {"style" : HoleStyle.SIMPLE, "endStyle" : HoleEndStyle.BLIND, "holeDiameter" : 4 * mm, "holeDepth" : 12 * mm, "isTappedThrough" : true, "tappedDepth" : 12 * mm, "tapClearance" : 3, "locations" : qUnion([Q0, Q1, Q2, Q3]), "scope" : qUnion([Q4])});
        }
        {
            var Q0;
            Q0=sQuery(id+"F44.wireOp",VERTEX,"E111.MirrorP");
            var Q1;
            Q1=sQuery(id+"F44.wireOp",VERTEX,"E112.MirrorP");
            var Q2;
            Q2=sQuery(id+"F44.wireOp",VERTEX,"E94");
            var Q3;
            Q3=sQuery(id+"F44.wireOp",VERTEX,"E92");
            var Q4;
            Q4=makeQuery(id+"F15.opExtrude","SWEPT_BODY",BODY,{"disambiguationData":[OSD([sQuery(id+"F14.wireOp",EDGE,"E30.bottom"),sQuery(id+"F14.wireOp",EDGE,"E30.top"),sQuery(id+"F14.wireOp",EDGE,"E30.left"),sQuery(id+"F14.wireOp",EDGE,"E30.right")])]});
            hole(context, id + "F48", {"style" : HoleStyle.SIMPLE, "endStyle" : HoleEndStyle.BLIND, "holeDiameter" : 4 * mm, "holeDepth" : 12 * mm, "isTappedThrough" : true, "tappedDepth" : 12 * mm, "tapClearance" : 3, "locations" : qUnion([Q0, Q1, Q2, Q3]), "scope" : qUnion([Q4])});
        }
        {
            var Q0;
            Q0=makeQuery(id+"F15.opExtrude","SWEPT_BODY",BODY,{"disambiguationData":[OSD([sQuery(id+"F14.wireOp",EDGE,"E30.bottom"),sQuery(id+"F14.wireOp",EDGE,"E30.top"),sQuery(id+"F14.wireOp",EDGE,"E30.left"),sQuery(id+"F14.wireOp",EDGE,"E30.right")])]});
            transform(context, id + "F49", {"entities" : qUnion([Q0]), "transformType" : TransformType.TRANSLATION_3D, "dx" : 0 * mm, "dy" : 0 * mm, "dz" : 700 * mm, "makeCopy" : true});
        }
    });
